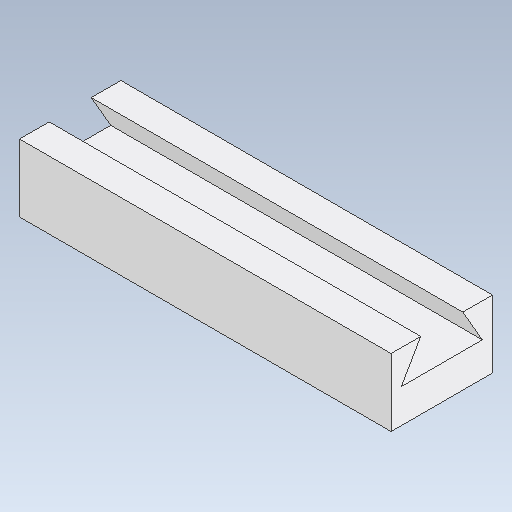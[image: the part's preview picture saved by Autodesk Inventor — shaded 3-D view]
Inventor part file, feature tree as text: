
AUTODESK INVENTOR PART (.ipt)
format: ipt  version: 2020.5 (Build 245400000, 400)  size: 98,816 bytes
history: native  units: mm
features: extrude x1, sketch x1
ambient origin geometry x8: Origin, YZ Plane, XZ Plane, XY Plane, X Axis, Y Axis, Z Axis, Center Point
bodies: Solid4 (feature_tree)
feature tree (2):
  extrude  "Extrusion3"  TaperAngle=60.0deg  [1 undecoded]
  sketch  "Sketch4"  dims[d31=60.0deg d32=60.0deg d33=10.0mm d34=12.0mm d35=110.0mm d36=0.0mm d43=10.0mm d44=30.0mm]
note: 1 required parameter value undecoded (feature->parameter linkage not recoverable at this tier; creation-order binding heuristic only, values carry confidence <= 0.55)
